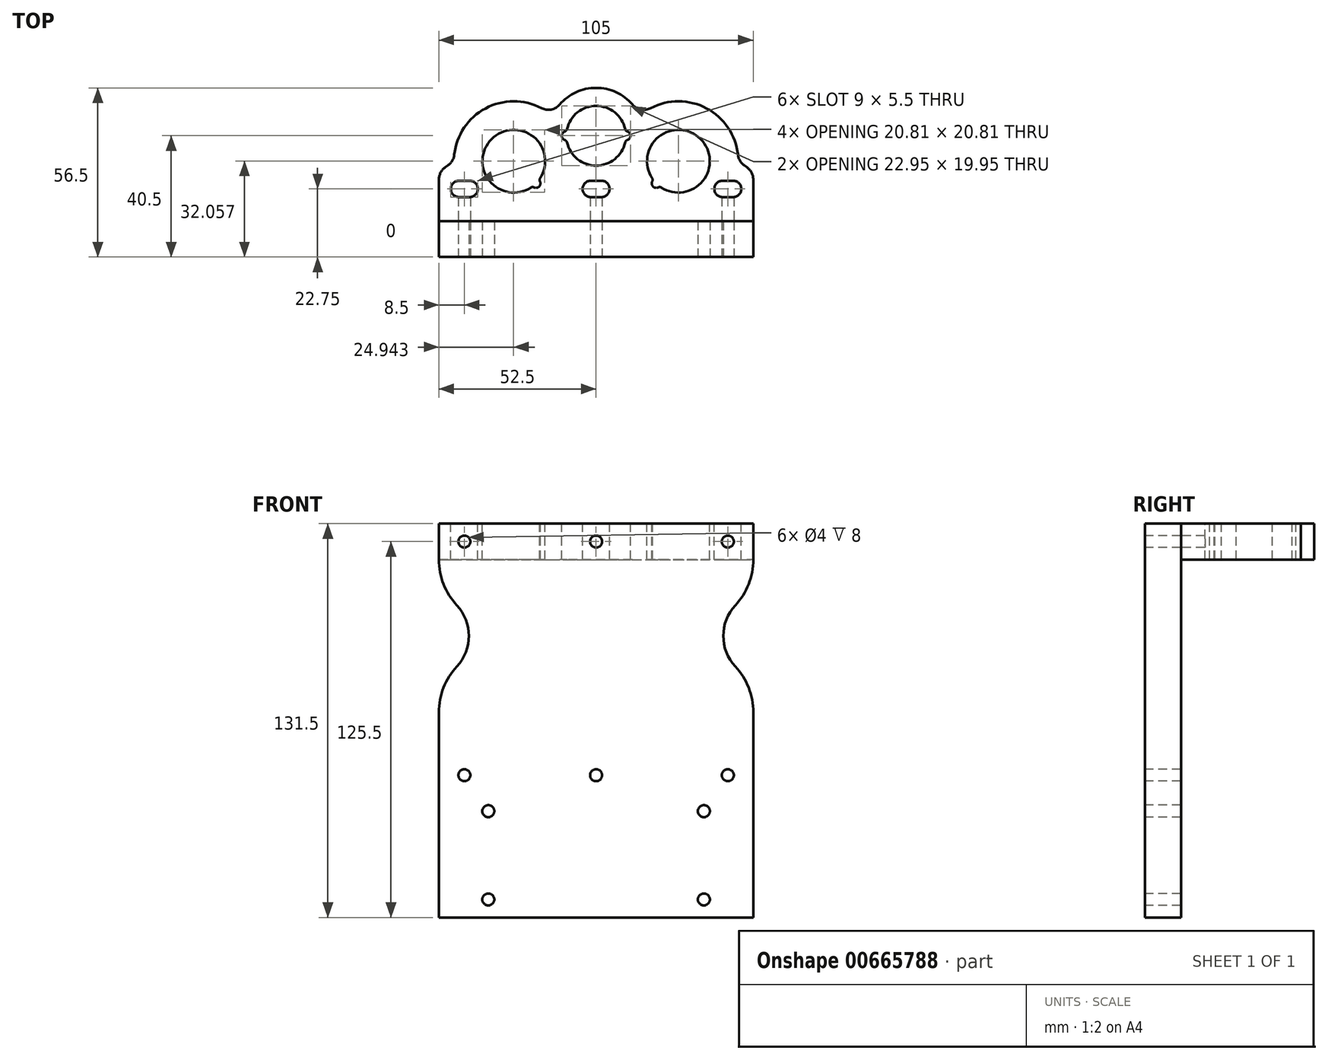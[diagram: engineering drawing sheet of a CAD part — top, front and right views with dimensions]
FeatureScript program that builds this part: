
annotation { "Feature Type Name" : "Feature", "Feature Type Description" : "" }
export const myFeature = defineFeature(function(context is Context, id is Id, definition is map)
    precondition{}
    {
        {
            var Q0;
            Q0=qCreatedBy(makeId("Front.planeOp"),FACE);
            var sketch = newSketch(context, id + "F0", { "sketchPlane" : qUnion([Q0])});
            skLineSegment(sketch, "E0.bottom", {"start": v(-52.5, 0) * mm, "end": v(52.5, 0) * mm});
            skLineSegment(sketch, "E0.top", {"start": v(-52.5, 104) * mm, "end": v(52.5, 104) * mm});
            skLineSegment(sketch, "E0.left", {"start": v(-52.5, 0) * mm, "end": v(-52.5, 104) * mm});
            skLineSegment(sketch, "E0.right", {"start": v(52.5, 0) * mm, "end": v(52.5, 104) * mm});
            skSolve(sketch);
        }
        {
            var Q0;
            Q0=qSketchRegion(id+"F0",true);
            extrude(context, id + "F1", {"entities" : qUnion([Q0]), "oppositeDirection" : true, "depth" : 12 * mm, "offsetDistance" : 25 * mm});
        }
        {
            var Q0;
            Q0=makeQuery(id+"F1.opExtrude","SWEPT_FACE",FACE,{"disambiguationData":[OSD([sQuery(id+"F0.wireOp",EDGE,"E0.top")])]});
            var sketch = newSketch(context, id + "F2", { "sketchPlane" : qUnion([Q0])});
            skLineSegment(sketch, "E1.top", {"start": v(27.5, 52) * mm, "end": v(11.12, 52) * mm, "construction": true});
            skLineSegment(sketch, "E2", {"start": v(0, 12) * mm, "end": v(0, 52) * mm, "construction": true});
            skPoint(sketch, "E3.centerSnap0", {"position": v(0, 32) * mm});
            skArc(sketch, "E4.filletArc", {"start": v(47.5, 32) * mm, "mid": v(41.64, 46.14) * mm, "end": v(27.5, 52) * mm});
            skArc(sketch, "E5.filletArc", {"start": v(-27.5, 52) * mm, "mid": v(-41.64, 46.14) * mm, "end": v(-47.5, 32) * mm});
            skArc(sketch, "E6", {"start": v(21.8, 23.22) * mm, "mid": v(34.9, 39.4) * mm, "end": v(18.72, 26.3) * mm});
            skArc(sketch, "E7.MirrorC", {"start": v(-21.8, 23.22) * mm, "mid": v(-34.9, 39.4) * mm, "end": v(-18.72, 26.3) * mm});
            skArc(sketch, "E8", {"start": v(11.12, 52) * mm, "mid": v(0, 56.5) * mm, "end": v(-11.12, 52) * mm});
            skArc(sketch, "E9", {"start": v(-9.74, 38.33) * mm, "mid": v(0, 30.53) * mm, "end": v(9.74, 38.33) * mm});
            skLineSegment(sketch, "E10", {"start": v(47.5, 12) * mm, "end": v(-47.5, 12) * mm});
            skLineSegment(sketch, "E11.bottom", {"start": v(47.5, 32) * mm, "end": v(52.5, 28.5) * mm});
            skLineSegment(sketch, "E11.top", {"start": v(47.5, 12) * mm, "end": v(52.5, 12) * mm});
            skLineSegment(sketch, "E11.right", {"start": v(52.5, 28.5) * mm, "end": v(52.5, 12) * mm});
            skLineSegment(sketch, "E12.bottom", {"start": v(42.25, 25.5) * mm, "end": v(45.75, 25.5) * mm});
            skLineSegment(sketch, "E12.top", {"start": v(42.25, 20) * mm, "end": v(45.75, 20) * mm});
            skArc(sketch, "E13", {"start": v(42.25, 25.5) * mm, "mid": v(39.5, 22.75) * mm, "end": v(42.25, 20) * mm});
            skArc(sketch, "E14", {"start": v(45.75, 20) * mm, "mid": v(48.5, 22.75) * mm, "end": v(45.75, 25.5) * mm});
            skArc(sketch, "E15.MirrorCS", {"start": v(-42.25, 25.5) * mm, "mid": v(-39.5, 22.75) * mm, "end": v(-42.25, 20) * mm});
            skLineSegment(sketch, "E16.MirrorCS", {"start": v(-42.25, 25.5) * mm, "end": v(-45.75, 25.5) * mm});
            skLineSegment(sketch, "E17.MirrorCS", {"start": v(-42.25, 20) * mm, "end": v(-45.75, 20) * mm});
            skArc(sketch, "E18.MirrorCS", {"start": v(-45.75, 20) * mm, "mid": v(-48.5, 22.75) * mm, "end": v(-45.75, 25.5) * mm});
            skLineSegment(sketch, "E19.MirrorCS", {"start": v(-47.5, 32) * mm, "end": v(-52.5, 28.5) * mm});
            skLineSegment(sketch, "E20.MirrorCS", {"start": v(-52.5, 28.5) * mm, "end": v(-52.5, 12) * mm});
            skLineSegment(sketch, "E21.MirrorCS", {"start": v(-47.5, 12) * mm, "end": v(-52.5, 12) * mm});
            skLineSegment(sketch, "E22.bottom", {"start": v(-1.75, 25.5) * mm, "end": v(1.75, 25.5) * mm});
            skLineSegment(sketch, "E22.top", {"start": v(-1.75, 20) * mm, "end": v(1.75, 20) * mm});
            skArc(sketch, "E23", {"start": v(-1.75, 25.5) * mm, "mid": v(-4.5, 22.75) * mm, "end": v(-1.75, 20) * mm});
            skArc(sketch, "E24", {"start": v(1.75, 20) * mm, "mid": v(4.5, 22.75) * mm, "end": v(1.75, 25.5) * mm});
            skLineSegment(sketch, "E25", {"start": v(-1.75, 22.75) * mm, "end": v(1.75, 22.75) * mm, "construction": true});
            skPoint(sketch, "E26", {"position": v(0, 22.75) * mm});
            skLineSegment(sketch, "E27", {"start": v(-44, 25.5) * mm, "end": v(-44, 20) * mm, "construction": true});
            skLineSegment(sketch, "E28", {"start": v(44, 20) * mm, "end": v(44, 25.5) * mm, "construction": true});
            skLineSegment(sketch, "E29.trimOffspring", {"start": v(-11.12, 52) * mm, "end": v(-27.5, 52) * mm, "construction": true});
            skLineSegment(sketch, "E30", {"start": v(-11.12, 52) * mm, "end": v(11.12, 52) * mm, "construction": true});
            skArc(sketch, "E31", {"start": v(-10.42, 41.93) * mm, "mid": v(-11.47, 40.5) * mm, "end": v(-10.42, 39.07) * mm});
            skArc(sketch, "E32.MirrorC", {"start": v(10.42, 41.93) * mm, "mid": v(11.47, 40.5) * mm, "end": v(10.42, 39.07) * mm});
            skArc(sketch, "E33.trimOffspring", {"start": v(9.74, 42.67) * mm, "mid": v(0, 50.48) * mm, "end": v(-9.74, 42.67) * mm});
            skPoint(sketch, "E34.visualSharp", {"position": v(-9.86, 42) * mm});
            skArc(sketch, "E34.filletArc", {"start": v(-10.42, 41.93) * mm, "mid": v(-9.98, 42.21) * mm, "end": v(-9.74, 42.67) * mm});
            skPoint(sketch, "E35.visualSharp", {"position": v(-9.86, 39) * mm});
            skArc(sketch, "E35.filletArc", {"start": v(-9.74, 38.33) * mm, "mid": v(-9.98, 38.79) * mm, "end": v(-10.42, 39.07) * mm});
            skPoint(sketch, "E36.visualSharp", {"position": v(9.86, 39) * mm});
            skArc(sketch, "E36.filletArc", {"start": v(10.42, 39.07) * mm, "mid": v(9.98, 38.79) * mm, "end": v(9.74, 38.33) * mm});
            skPoint(sketch, "E37.visualSharp", {"position": v(9.86, 42) * mm});
            skArc(sketch, "E37.filletArc", {"start": v(9.74, 42.67) * mm, "mid": v(9.98, 42.21) * mm, "end": v(10.42, 41.93) * mm});
            skArc(sketch, "E38", {"start": v(-20.79, 23.26) * mm, "mid": v(-19.03, 23.53) * mm, "end": v(-18.76, 25.29) * mm});
            skLineSegment(sketch, "E39", {"start": v(-27.5, 32) * mm, "end": v(-20.1, 24.6) * mm, "construction": true});
            skArc(sketch, "E40.MirrorCS", {"start": v(20.79, 23.26) * mm, "mid": v(19.03, 23.53) * mm, "end": v(18.76, 25.29) * mm});
            skPoint(sketch, "E41.visualSharp", {"position": v(-21.23, 23.61) * mm});
            skArc(sketch, "E41.filletArc", {"start": v(-20.79, 23.26) * mm, "mid": v(-21.3, 23.38) * mm, "end": v(-21.8, 23.22) * mm});
            skPoint(sketch, "E42.visualSharp", {"position": v(-19.11, 25.73) * mm});
            skArc(sketch, "E42.filletArc", {"start": v(-18.72, 26.3) * mm, "mid": v(-18.88, 25.8) * mm, "end": v(-18.76, 25.29) * mm});
            skPoint(sketch, "E43.visualSharp", {"position": v(19.11, 25.73) * mm});
            skArc(sketch, "E43.filletArc", {"start": v(18.76, 25.29) * mm, "mid": v(18.88, 25.8) * mm, "end": v(18.72, 26.3) * mm});
            skPoint(sketch, "E44.visualSharp", {"position": v(21.23, 23.61) * mm});
            skArc(sketch, "E44.filletArc", {"start": v(21.8, 23.22) * mm, "mid": v(21.3, 23.38) * mm, "end": v(20.79, 23.26) * mm});
            skArc(sketch, "E45", {"start": v(-27.5, 52) * mm, "mid": v(-22.74, 51.43) * mm, "end": v(-18.25, 49.73) * mm});
            skArc(sketch, "E46", {"start": v(-11.12, 52) * mm, "mid": v(-11.65, 51.47) * mm, "end": v(-12.15, 50.91) * mm});
            skArc(sketch, "E47.MirrorCS", {"start": v(27.5, 52) * mm, "mid": v(22.74, 51.43) * mm, "end": v(18.25, 49.73) * mm});
            skArc(sketch, "E48.MirrorCS", {"start": v(11.12, 52) * mm, "mid": v(11.65, 51.47) * mm, "end": v(12.15, 50.91) * mm});
            skPoint(sketch, "E49.visualSharp", {"position": v(-14.52, 47.22) * mm});
            skArc(sketch, "E49.filletArc", {"start": v(-18.25, 49.73) * mm, "mid": v(-15, 49.26) * mm, "end": v(-12.15, 50.91) * mm});
            skPoint(sketch, "E50.visualSharp", {"position": v(14.52, 47.22) * mm});
            skArc(sketch, "E50.filletArc", {"start": v(12.15, 50.91) * mm, "mid": v(15, 49.26) * mm, "end": v(18.25, 49.73) * mm});
            skSolve(sketch);
        }
        {
            var Q0;
            Q0=qSketchRegion(id+"F2",true);
            extrude(context, id + "F3", {"entities" : qUnion([Q0]), "oppositeDirection" : true, "depth" : 12 * mm, "offsetDistance" : 25 * mm});
        }
        {
            var Q0;
            Q0=makeQuery(id+"F3.opExtrude","SWEPT_EDGE",EDGE,{"disambiguationData":[OSD([sQuery(id+"F2.wireOp",EDGE,"E5.filletArc"),sQuery(id+"F2.wireOp",EDGE,"E19.MirrorCS")])]});
            var Q1;
            Q1=makeQuery(id+"F3.opExtrude","SWEPT_EDGE",EDGE,{"disambiguationData":[OSD([sQuery(id+"F2.wireOp",EDGE,"E19.MirrorCS"),sQuery(id+"F2.wireOp",EDGE,"E20.MirrorCS")])]});
            var Q2;
            Q2=makeQuery(id+"F3.opExtrude","SWEPT_EDGE",EDGE,{"disambiguationData":[OSD([sQuery(id+"F2.wireOp",EDGE,"E4.filletArc"),sQuery(id+"F2.wireOp",EDGE,"E11.bottom")])]});
            var Q3;
            Q3=makeQuery(id+"F3.opExtrude","SWEPT_EDGE",EDGE,{"disambiguationData":[OSD([sQuery(id+"F2.wireOp",EDGE,"E11.bottom"),sQuery(id+"F2.wireOp",EDGE,"E11.right")])]});
            fillet(context, id + "F4", {"entities" : qUnion([Q0, Q1, Q2, Q3]), "radius" : 5 * mm, "tangentPropagation" : true, "allowEdgeOverflow" : false});
        }
        {
            var Q0;
            Q0=makeQuery(id+"F1.opExtrude","CAP_FACE",FACE,{"disambiguationData":[OSD([sQuery(id+"F0.wireOp",EDGE,"E0.bottom"),sQuery(id+"F0.wireOp",EDGE,"E0.top"),sQuery(id+"F0.wireOp",EDGE,"E0.left"),sQuery(id+"F0.wireOp",EDGE,"E0.right")])],"isStart":true});
            var sketch = newSketch(context, id + "F5", { "sketchPlane" : qUnion([Q0])});
            skLineSegment(sketch, "E51.bottom", {"start": v(-52.5, 0) * mm, "end": v(52.5, 0) * mm});
            skLineSegment(sketch, "E51.top", {"start": v(-52.5, -27.5) * mm, "end": v(52.5, -27.5) * mm});
            skLineSegment(sketch, "E51.left", {"start": v(-52.5, 0) * mm, "end": v(-52.5, -27.5) * mm});
            skLineSegment(sketch, "E51.right", {"start": v(52.5, 0) * mm, "end": v(52.5, -27.5) * mm});
            skSolve(sketch);
        }
        {
            var Q0;
            Q0=qSketchRegion(id+"F5",true);
            var Q1;
            Q1=makeQuery(id+"F1.opExtrude","CAP_FACE",FACE,{"disambiguationData":[OSD([sQuery(id+"F0.wireOp",EDGE,"E0.bottom"),sQuery(id+"F0.wireOp",EDGE,"E0.top"),sQuery(id+"F0.wireOp",EDGE,"E0.left"),sQuery(id+"F0.wireOp",EDGE,"E0.right")])],"isStart":false});
            extrude(context, id + "F6", {"entities" : qUnion([Q0]), "operationType" : NewBodyOperationType.ADD, "endBound" : BoundingType.UP_TO_SURFACE, "oppositeDirection" : true, "depth" : 18 * mm, "endBoundEntityFace" : qUnion([Q1]), "offsetDistance" : 25 * mm});
        }
        {
            var Q0;
            Q0=makeQuery(id+"F1.opExtrude","CAP_FACE",FACE,{"disambiguationData":[OSD([sQuery(id+"F0.wireOp",EDGE,"E0.bottom"),sQuery(id+"F0.wireOp",EDGE,"E0.top"),sQuery(id+"F0.wireOp",EDGE,"E0.left"),sQuery(id+"F0.wireOp",EDGE,"E0.right")])],"isStart":true});
            var sketch = newSketch(context, id + "F7", { "sketchPlane" : qUnion([Q0])});
            skCircle(sketch, "E52", {"center": v(-44, 98) * mm, "radius": 2 * mm});
            skCircle(sketch, "E53", {"center": v(44, 98) * mm, "radius": 2 * mm});
            skCircle(sketch, "E54", {"center": v(0, 98) * mm, "radius": 2 * mm});
            skCircle(sketch, "E55.MirrorC", {"center": v(44, 20) * mm, "radius": 2 * mm});
            skCircle(sketch, "E56.MirrorC", {"center": v(0, 20) * mm, "radius": 2 * mm});
            skCircle(sketch, "E57.MirrorC", {"center": v(-44, 20) * mm, "radius": 2 * mm});
            skCircle(sketch, "E58", {"center": v(-36, -21.5) * mm, "radius": 2 * mm});
            skCircle(sketch, "E59", {"center": v(36, -21.5) * mm, "radius": 2 * mm});
            skCircle(sketch, "E60.0.1.0", {"center": v(36, 8) * mm, "radius": 2 * mm});
            skCircle(sketch, "E60.0.1.1", {"center": v(-36, 8) * mm, "radius": 2 * mm});
            skLineSegment(sketch, "E60.direction1", {"start": v(-36, -21.5) * mm, "end": v(-14, -21.5) * mm, "construction": true});
            skLineSegment(sketch, "E60.direction2", {"start": v(-36, -21.5) * mm, "end": v(-36, 8) * mm, "construction": true});
            skLineSegment(sketch, "E61", {"start": v(-44, 20) * mm, "end": v(0, 20) * mm, "construction": true});
            skLineSegment(sketch, "E62", {"start": v(44, 20) * mm, "end": v(0, 20) * mm, "construction": true});
            skLineSegment(sketch, "E63", {"start": v(0, 20) * mm, "end": v(0, -27.5) * mm, "construction": true});
            skPoint(sketch, "E63.endSnap0", {"position": v(0, -27.5) * mm});
            skSolve(sketch);
        }
        {
            var Q0;
            Q0=qSketchRegion(id+"F7",true);
            extrude(context, id + "F8", {"entities" : qUnion([Q0]), "operationType" : NewBodyOperationType.REMOVE, "oppositeDirection" : true, "depth" : 25 * mm, "offsetDistance" : 25 * mm});
        }
        {
            var Q0;
            Q0=makeQuery(id+"F6.boolean.opBoolean","MERGE",FACE,{"derivedFrom":[makeQuery(id+"F1.opExtrude","CAP_FACE",FACE,{"disambiguationData":[OSD([sQuery(id+"F0.wireOp",EDGE,"E0.bottom"),sQuery(id+"F0.wireOp",EDGE,"E0.top"),sQuery(id+"F0.wireOp",EDGE,"E0.left"),sQuery(id+"F0.wireOp",EDGE,"E0.right")])],"isStart":true}),makeQuery(id+"F6.opExtrude","CAP_FACE",FACE,{"disambiguationData":[OSD([sQuery(id+"F5.wireOp",EDGE,"E51.bottom"),sQuery(id+"F5.wireOp",EDGE,"E51.top"),sQuery(id+"F5.wireOp",EDGE,"E51.left"),sQuery(id+"F5.wireOp",EDGE,"E51.right")])],"isStart":true})]});
            var sketch = newSketch(context, id + "F9", { "sketchPlane" : qUnion([Q0])});
            skCircle(sketch, "E64", {"center": v(-57.5, 66.5) * mm, "radius": 15 * mm});
            skLineSegment(sketch, "E65", {"start": v(-52.5, 41) * mm, "end": v(52.5, 41) * mm, "construction": true});
            skLineSegment(sketch, "E66", {"start": v(0, 41) * mm, "end": v(0, 104) * mm, "construction": true});
            skCircle(sketch, "E67.MirrorC", {"center": v(57.5, 66.5) * mm, "radius": 15 * mm});
            skSolve(sketch);
        }
        {
            var Q0;
            Q0=qSketchRegion(id+"F9",true);
            extrude(context, id + "F10", {"entities" : qUnion([Q0]), "operationType" : NewBodyOperationType.REMOVE, "oppositeDirection" : true, "depth" : 25 * mm, "offsetDistance" : 25 * mm});
        }
        {
            var Q0;
            Q0=makeQuery(id+"F10.boolean.opBoolean","INTERSECT",EDGE,{"disambiguationData":[OD(0.0)],"derivedFrom":[makeQuery(id+"F6.boolean.opBoolean","MERGE",FACE,{"derivedFrom":[makeQuery(id+"F1.opExtrude","SWEPT_FACE",FACE,{"disambiguationData":[OSD([sQuery(id+"F0.wireOp",EDGE,"E0.left")])]}),makeQuery(id+"F6.opExtrude","SWEPT_FACE",FACE,{"disambiguationData":[OSD([sQuery(id+"F5.wireOp",EDGE,"E51.left")])]})]}),makeQuery(id+"F10.opExtrude","SWEPT_FACE",FACE,{"disambiguationData":[OSD([sQuery(id+"F9.wireOp",EDGE,"E64")])]})]});
            var Q1;
            Q1=makeQuery(id+"F10.boolean.opBoolean","INTERSECT",EDGE,{"disambiguationData":[OD(1.0)],"derivedFrom":[makeQuery(id+"F6.boolean.opBoolean","MERGE",FACE,{"derivedFrom":[makeQuery(id+"F1.opExtrude","SWEPT_FACE",FACE,{"disambiguationData":[OSD([sQuery(id+"F0.wireOp",EDGE,"E0.left")])]}),makeQuery(id+"F6.opExtrude","SWEPT_FACE",FACE,{"disambiguationData":[OSD([sQuery(id+"F5.wireOp",EDGE,"E51.left")])]})]}),makeQuery(id+"F10.opExtrude","SWEPT_FACE",FACE,{"disambiguationData":[OSD([sQuery(id+"F9.wireOp",EDGE,"E64")])]})]});
            var Q2;
            Q2=makeQuery(id+"F10.boolean.opBoolean","INTERSECT",EDGE,{"disambiguationData":[OD(0.0)],"derivedFrom":[makeQuery(id+"F6.boolean.opBoolean","MERGE",FACE,{"derivedFrom":[makeQuery(id+"F1.opExtrude","SWEPT_FACE",FACE,{"disambiguationData":[OSD([sQuery(id+"F0.wireOp",EDGE,"E0.right")])]}),makeQuery(id+"F6.opExtrude","SWEPT_FACE",FACE,{"disambiguationData":[OSD([sQuery(id+"F5.wireOp",EDGE,"E51.right")])]})]}),makeQuery(id+"F10.opExtrude","SWEPT_FACE",FACE,{"disambiguationData":[OSD([sQuery(id+"F9.wireOp",EDGE,"E67.MirrorC")])]})]});
            var Q3;
            Q3=makeQuery(id+"F10.boolean.opBoolean","INTERSECT",EDGE,{"disambiguationData":[OD(1.0)],"derivedFrom":[makeQuery(id+"F6.boolean.opBoolean","MERGE",FACE,{"derivedFrom":[makeQuery(id+"F1.opExtrude","SWEPT_FACE",FACE,{"disambiguationData":[OSD([sQuery(id+"F0.wireOp",EDGE,"E0.right")])]}),makeQuery(id+"F6.opExtrude","SWEPT_FACE",FACE,{"disambiguationData":[OSD([sQuery(id+"F5.wireOp",EDGE,"E51.right")])]})]}),makeQuery(id+"F10.opExtrude","SWEPT_FACE",FACE,{"disambiguationData":[OSD([sQuery(id+"F9.wireOp",EDGE,"E67.MirrorC")])]})]});
            fillet(context, id + "F11", {"entities" : qUnion([Q0, Q1, Q2, Q3]), "radius" : 22.5 * mm, "tangentPropagation" : true, "allowEdgeOverflow" : false});
        }
    });
